# Revit family: Arper_Aava-02_chair_sled_wood_front-face-upholstery_7633
name_source: partatom
category: Furniture
units: mm (PartAtom-declared; Revit-internal decimal feet)

## family parameters
Always vertical = Yes
Cut with Voids When Loaded = No
OmniClass Number = 23.40.20.00
OmniClass Title = General Furniture and Specialties
Room Calculation Point = No
Shared = No
Work Plane-Based = No

## types (1)
- Arper_Aava-02_chair_sled_wood_front-face-upholstery_7633
    Default Elevation = 0 mm  [stored 0 ft]
    Description = Chair on a sled base in chromed or powder-coated steel. Shell in 
plywood with a reconstituted oak or walnut finish, with front 
upholstery in fabric, leather, coated fabric or customer’s own 
material. Glides are also available, with felt insert for wood floors.
    Manufacturer = ARPER s.p.a.
    Model = Aava 02
    URL = http://www.arper.com

note: [stored X ft] marks values corroborated as IEEE doubles in the binary element streams (Revit-internal decimal feet)
